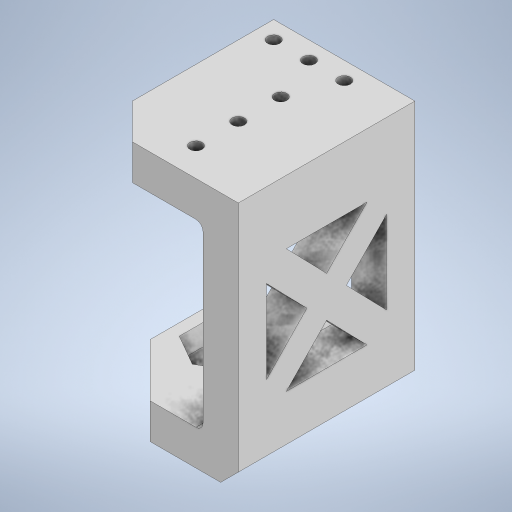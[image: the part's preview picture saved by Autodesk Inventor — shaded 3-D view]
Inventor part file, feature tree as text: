
AUTODESK INVENTOR PART (.ipt)
format: ipt  version: 2023 (Build 270158000, 158)  size: 339,968 bytes
history: native  units: mm
features: extrude x8, sketch x7, chamfer x3, other x2, fillet x1, projected_geometry x1
ambient origin geometry x8: Origin, YZ Plane, XZ Plane, XY Plane, X Axis, Y Axis, Z Axis, Center Point
bodies: Body1 (feature_tree)
feature tree (22):
  other  "솔리드1"
  extrude  "돌출1"  Depth=71.0mm
  other  "작업 평면1"
  extrude  "돌출5"  Depth=10.0mm
  fillet  "모깎기1"  Radius=10.0mm
  extrude  "돌출6"  Depth=30.0mm
  chamfer  "모따기1"  Distance=50.0mm
  extrude  "돌출7"  Depth=6.0mm
  sketch  "스케치14"
  extrude  "돌출12"  Depth=8.0mm
  extrude  "돌출13"  Depth=4.0mm
  extrude  "돌출14"  Depth=4.0mm
  chamfer  "모따기3"  Distance=10.0mm
  chamfer  "모따기4"  Distance=2.0mm
  extrude  "돌출15"  Depth=10.0mm
  sketch  "스케치1"
  sketch  "스케치5"
  projected_geometry  "투영된 루프1"
  sketch  "스케치6"
  sketch  "스케치7"
  sketch  "스케치15"
  sketch  "스케치16"
